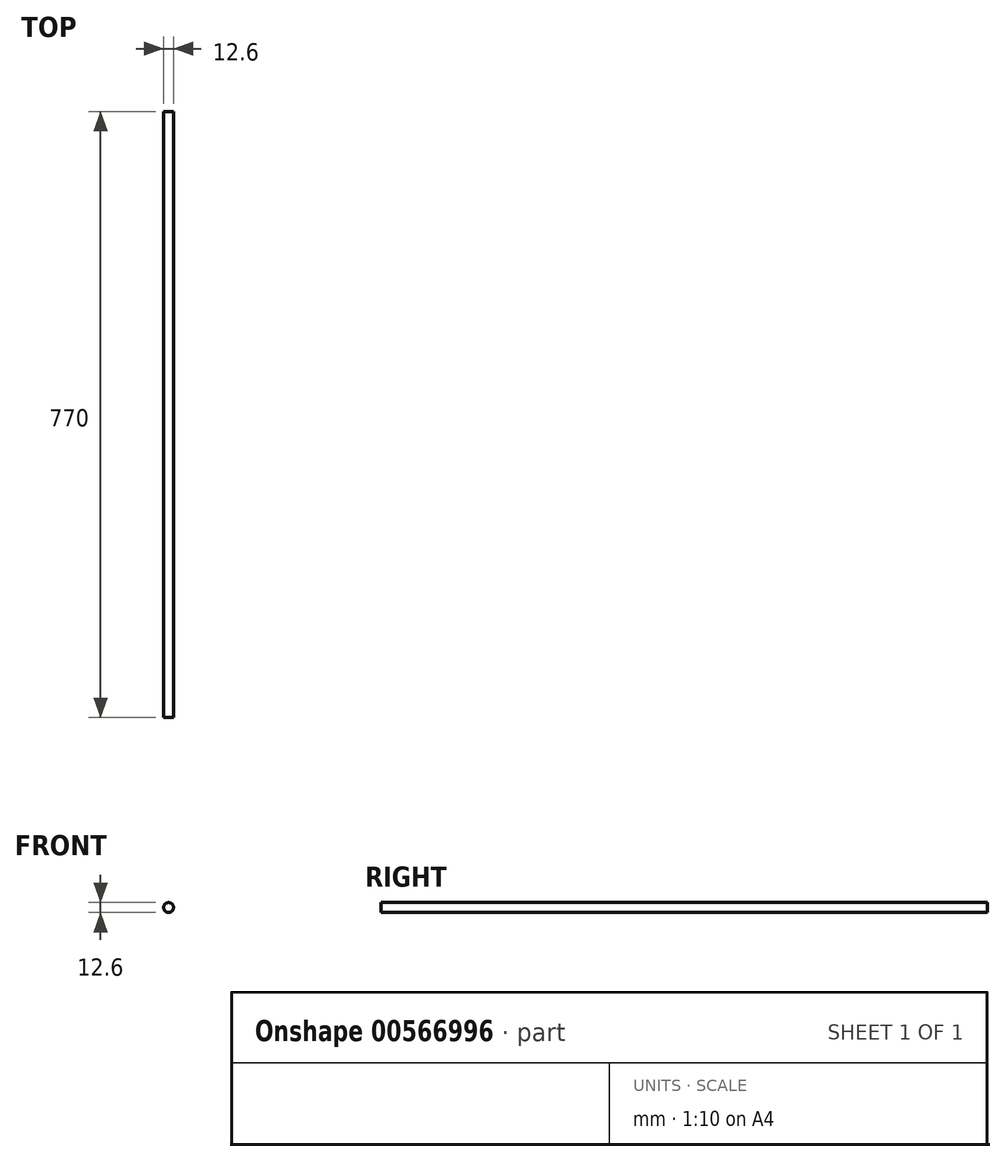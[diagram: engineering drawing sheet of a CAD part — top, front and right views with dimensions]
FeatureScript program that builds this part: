
annotation { "Feature Type Name" : "Feature", "Feature Type Description" : "" }
export const myFeature = defineFeature(function(context is Context, id is Id, definition is map)
    precondition{}
    {
        {
            var Q0;
            Q0=qCreatedBy(makeId("Front.planeOp"),FACE);
            var sketch = newSketch(context, id + "F0", { "sketchPlane" : qUnion([Q0])});
            skCircle(sketch, "E0", {"center": v(0, 0) * mm, "radius": 6.3 * mm});
            skSolve(sketch);
        }
        {
            var Q0;
            Q0 = qSketchRegion(id + "F0", true);
            extrude(context, id + "F1", {"entities" : qUnion([Q0]), "depth" : 770 * mm, "offsetDistance" : 25 * mm});
        }
    });
